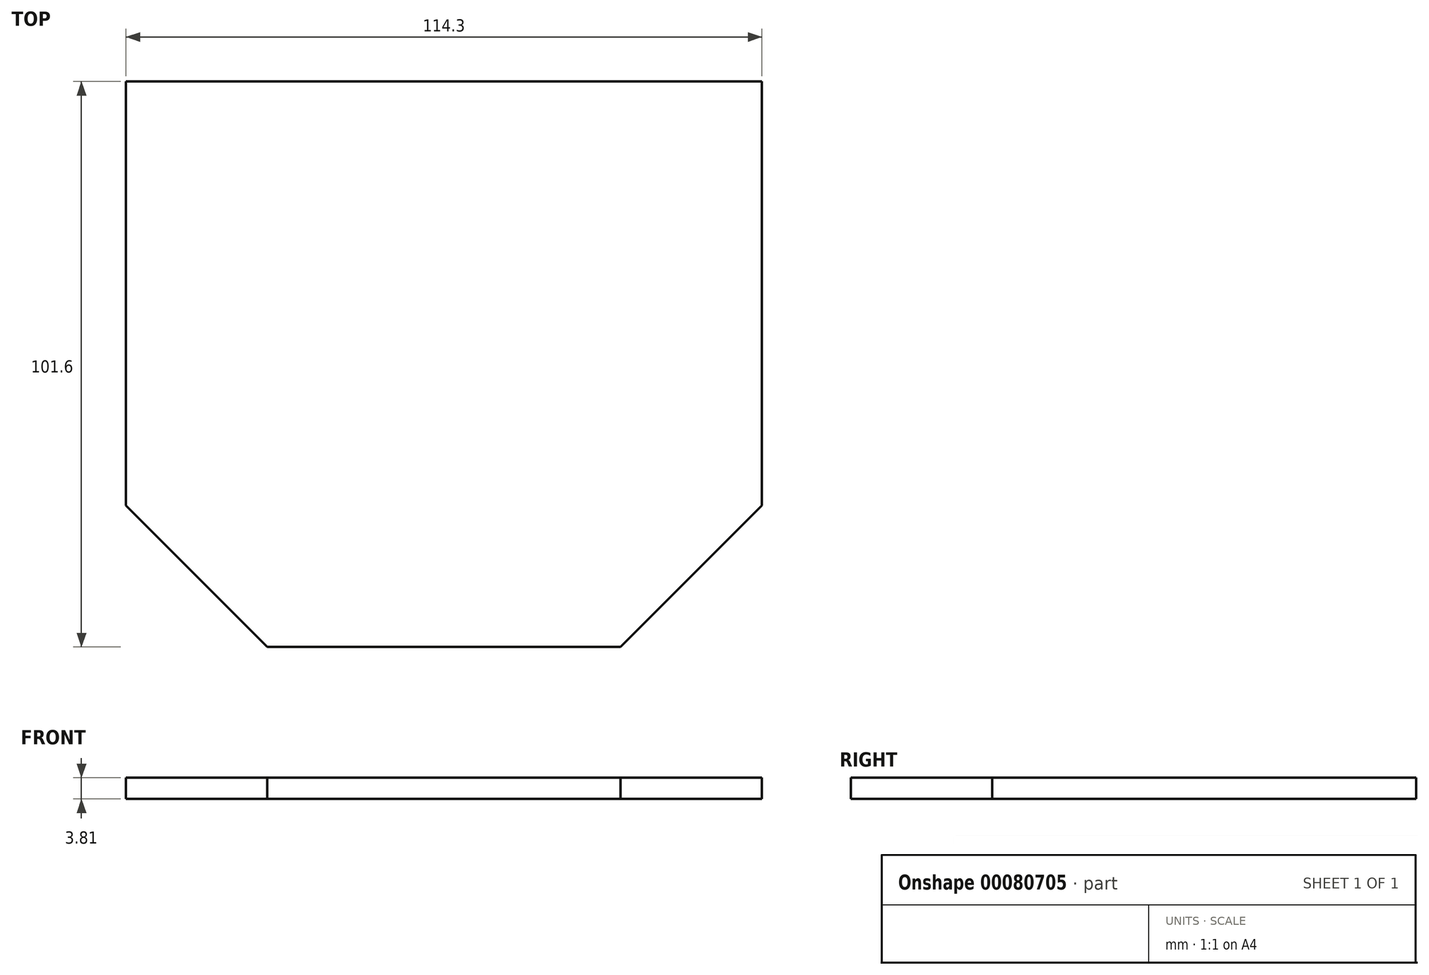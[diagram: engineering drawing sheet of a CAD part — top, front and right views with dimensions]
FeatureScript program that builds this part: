
annotation { "Feature Type Name" : "Feature", "Feature Type Description" : "" }
export const myFeature = defineFeature(function(context is Context, id is Id, definition is map)
    precondition{}
    {
        {
            var Q0;
            Q0=qCreatedBy(makeId("Top.planeOp"),FACE);
            var sketch = newSketch(context, id + "F0", { "sketchPlane" : qUnion([Q0])});
            skLineSegment(sketch, "E0.bottom", {"start": v(57.15, -38.1) * mm, "end": v(-57.15, -38.1) * mm, "construction": true});
            skLineSegment(sketch, "E0.top", {"start": v(57.15, 38.1) * mm, "end": v(-57.15, 38.1) * mm});
            skLineSegment(sketch, "E0.left", {"start": v(57.15, -38.1) * mm, "end": v(57.15, 38.1) * mm});
            skLineSegment(sketch, "E0.right", {"start": v(-57.15, -38.1) * mm, "end": v(-57.15, 38.1) * mm});
            skPoint(sketch, "E0.middle", {"position": v(0, 0) * mm});
            skLineSegment(sketch, "E1", {"start": v(0, -38.1) * mm, "end": v(0, -63.5) * mm, "construction": true});
            skPoint(sketch, "E1.endSnap0", {"position": v(0, -38.1) * mm});
            skLineSegment(sketch, "E2", {"start": v(0, -63.5) * mm, "end": v(-31.75, -63.5) * mm});
            skLineSegment(sketch, "E3", {"start": v(0, -63.5) * mm, "end": v(31.75, -63.5) * mm});
            skLineSegment(sketch, "E4", {"start": v(31.75, -63.5) * mm, "end": v(57.15, -38.1) * mm});
            skLineSegment(sketch, "E5", {"start": v(-31.75, -63.5) * mm, "end": v(-57.15, -38.1) * mm});
            skSolve(sketch);
        }
        {
            var Q0;
            Q0=makeQuery(id+"F0.imprint","IMPRINT",FACE,{"disambiguationData":[TD([[makeQuery(id+"F0.imprint","IMPRINT",EDGE,{"derivedFrom":sQuery(id+"F0.wireOp",EDGE,"E0.top")}),1.0]])]});
            extrude(context, id + "F1", {"entities" : qUnion([Q0]), "depth" : 3.8 * mm});
        }
    });
